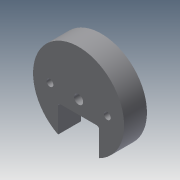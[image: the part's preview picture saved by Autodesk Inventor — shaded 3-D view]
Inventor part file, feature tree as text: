
AUTODESK INVENTOR PART (.ipt)
format: ipt  version: 2013 (Build 170138000, 138)  size: 140,800 bytes
history: native  units: mm
features: sketch x12, extrude x10, fillet x1
ambient origin geometry x8: Origin, YZ Plane, XZ Plane, XY Plane, X Axis, Y Axis, Z Axis, Center Point
bodies: Solid1 (feature_tree)
feature tree (23):
  extrude  "Extrusion1"  Depth=10.0mm TaperAngle=0.0deg
  extrude  "Extrusion2"  Depth=10.0mm TaperAngle=0.0deg
  extrude  "Extrusion3"  Depth=3.0mm
  sketch  "Sketch4"  dims[d9=10.0mm d10=0.0mm d11=10.0mm]
  sketch  "Sketch5"  dims[d12=10.0mm d13=0.0mm d14=6.0mm]
  extrude  "Extrusion4"  Depth=10.0mm
  extrude  "Extrusion5"  Depth=6.0mm
  extrude  "Extrusion6"  Depth=18.0mm
  extrude  "Extrusion7"  Depth=10.0mm TaperAngle=0.0deg
  extrude  "Extrusion8"  Depth=2.0mm
  extrude  "Extrusion9"  Depth=8.0mm TaperAngle=0.0deg
  extrude  "Extrusion10"  Depth=4.0mm
  fillet  "Fillet1"  Radius=10.0mm
  sketch  "Sketch1"  dims[d0=40.0mm d1=10.0mm d2=0.0mm]
  sketch  "Sketch2"  dims[d3=12.0mm d4=10.0mm d5=0.0mm]
  sketch  "Sketch3"  dims[d7=3.0mm d8=3.0mm]
  sketch  "Sketch6"  dims[d15=2.0mm d16=0.0mm d17=18.0mm]
  sketch  "Sketch7"  dims[d18=10.0mm d19=10.0mm d20=0.0mm]
  sketch  "Sketch8"  dims[d21=18.0mm d25=2.0mm]
  sketch  "Sketch9"  dims[d26=10.0mm d27=0.0mm d28=8.0mm d29=0.0mm]
  sketch  "Sketch10"  dims[d30=8.0mm d31=0.0mm d32=4.0mm d33=10.0mm d34=0.0mm]
  sketch  "Sketch11"  dims[d35=1.0mm]
  sketch  "Sketch12"
